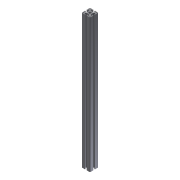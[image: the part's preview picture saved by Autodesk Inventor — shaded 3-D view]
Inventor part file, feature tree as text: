
AUTODESK INVENTOR PART (.ipt)
format: ipt  version: 2016 (Build 200138000, 138)  size: 183,808 bytes
history: native  units: mm
features: other x42, sketch x5, hole x4, extrude x1
ambient origin geometry x8: Origin, YZ Plane, XZ Plane, XY Plane, X Axis, Y Axis, Z Axis, Center Point
bodies: Solid1 (feature_tree)
feature tree (52):
  extrude  "Extrusion1"  [1 undecoded]
  hole  "Drilling 1"  [1 undecoded]
  hole  "Drilling 2"  [1 undecoded]
  hole  "Drilling 3"  [1 undecoded]
  hole  "Drilling 4"  [1 undecoded]
  other  "side_4d_XY"
  other  "side_4d_YZ"
  other  "side_4d_ZX"
  other  "side_4d_X"
  other  "side_4d_Y"
  other  "side_4d_Z"
  other  "side_4d_Center"
  other  "side_1a_XY"
  other  "side_1a_YZ"
  other  "side_1a_ZX"
  other  "side_1a_X"
  other  "side_1a_Y"
  other  "side_1a_Z"
  other  "side_1a_Center"
  other  "side_2b_XY"
  other  "side_2b_YZ"
  other  "side_2b_ZX"
  other  "side_2b_X"
  other  "side_2b_Y"
  other  "side_2b_Z"
  other  "side_2b_Center"
  other  "side_3c_XY"
  other  "side_3c_YZ"
  other  "side_3c_ZX"
  other  "side_3c_X"
  other  "side_3c_Y"
  other  "side_3c_Z"
  other  "side_3c_Center"
  other  "end_XY"
  other  "end_YZ"
  other  "end_ZX"
  other  "end_X"
  other  "end_Y"
  other  "end_Z"
  other  "end_Center"
  other  "start_XY"
  other  "start_YZ"
  other  "start_ZX"
  other  "start_X"
  other  "start_Y"
  other  "start_Z"
  other  "start_Center"
  sketch  "Skizze_1"  dims[d0=640.0mm d1=0.0mm]
  sketch  "Sketch2"  dims[d2=5.0mm d3=6.0mm d4=4.0mm d5=2.0mm d6=90.0deg d7=6000.0mm d8=0.0mm]
  sketch  "Sketch3"  dims[d9=5.0mm d10=6.0mm d11=4.0mm d12=2.0mm d13=90.0deg d14=6000.0mm d15=0.0mm]
  sketch  "Sketch4"  dims[d16=5.0mm d17=6.0mm d18=4.0mm d19=2.0mm d20=90.0deg d21=6000.0mm d22=0.0mm]
  sketch  "Sketch5"  dims[d23=5.0mm d24=6.0mm d25=4.0mm d26=2.0mm d27=90.0deg d28=6000.0mm d29=0.0mm]
note: 5 required parameter values undecoded (feature->parameter linkage not recoverable at this tier; creation-order binding heuristic only, values carry confidence <= 0.55)
